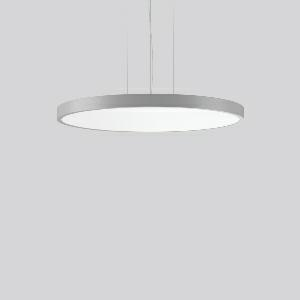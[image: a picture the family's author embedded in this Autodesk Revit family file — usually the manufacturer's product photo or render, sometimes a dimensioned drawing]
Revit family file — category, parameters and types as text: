
# Revit family: triona_round_p_312390_004_76_7f1f
name_source: partatom
category: Lighting Fixtures
units: mm (PartAtom-declared; Revit-internal decimal feet)

## family parameters
Cut with Voids When Loaded = No
Host = Face
Light Source = No
Part Type = Normal
Room Calculation Point = No
Round Connector Dimension = Use Diameter
Shared = No

## types (1)
- TRIONA round P (1 x LED Modul 830, 12400 lm, 3000)
    Apparent Load = 133 VA
    CIE Flux Codes = 49 80 96 71 100
    Color Rendering = 80
    Color Temperature = 3000
    Default Elevation = 1800 mm
    Description = Series: TRIONA round
Decorative round LED pendant-mounted surface luminaire. Flat, seamless frame: aluminium extrusion profile, powder coated. Cover made of sheet steel, powder-coated. Canopy made of aluminium, powder-coated. Direct light emission through a diffuser plastic opal. Indirect light emission through a flush diffuser made of satin-finish plastic. Lightguide and diffuser made of non-yellowing plastic (PMMA). Lateral light emission (RZB SIDELITE technology) for above-average homogeneous light distribution. Direct 70%, indirect 30% light emission. 3-point steel cable suspension, steplessly adjustable. Easy installation with transparent, adjustable pendant cable and canopy with magnetic fixing. Driver integrated. 
Colour: silver, matt (approx. RAL 9006)
Diameter: 845 mm
Height: 52 mm
Suspension length: 500-1200 mm
Lamp: LED
Socket: without socket
Colour temperature: 3000K
Colour rendering index (CRI): 80
System power: 133 W
Rated luminous flux: 12400 lm
Luminous efficiency: 93 lm/W
Control gear: Converter, dimmable, DALI
Protection class: I
Type of protection: IP 20
    Height = 52 mm  [stored 0.170604 ft]
    Lamp = 1 x LED Modul 830
    Lamp Light Flux = 12400 lm
    Lamp count = 1
    Length = 845 mm
    Lifetime = 50000 h
    Luminous efficacy = 93 lm/W
    Manufacturer = RZB
    ModVariant = No
    Model = 312390.004.76
    Mounting Place = Ceiling
    Mounting Type = Pendant
    Number of Poles = 1
    OnlyDefault = Yes
    Power Factor = 1
    Product Name = TRIONA round P
    Product group = Pendant modular luminaires
    ProductGroupID = 906
    Protection Class = Protection class I
    Protection Degree = IP 20
    RLX_Detail_Level = 1
    RLX_Emergency_Light_Flux = 0 lm
    RLX_Emergency_Type = 0
    RLX_Emergency_Type_DB = No
    RlxData = <blob elided: 38825 chars, md5=25ca4cef>
    Socket = socket
    Standby Power = 0 W
    System Light Flux = 12400 lm
    System Power = 133 W
    Type Comments = Product without accessories
    Type Image = 312390.004.jpg
    URL = http://relux.com
    VarID = ---
    Voltage = 230 V
    Voltage Range = 220-240 V
    Weight = 0.00 kg
    Width = 0 mm  [stored 0 ft]

note: [stored X ft] marks values corroborated as IEEE doubles in the binary element streams (Revit-internal decimal feet)

## geometry (parser evidence)
native form markers: Blend x4, Sweep x15
no freeform markers — native parametric forms only
